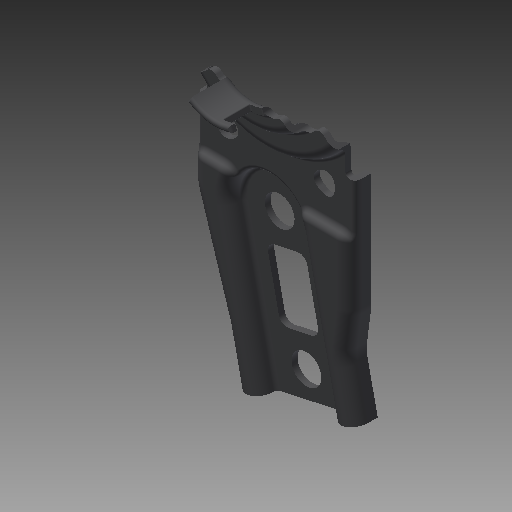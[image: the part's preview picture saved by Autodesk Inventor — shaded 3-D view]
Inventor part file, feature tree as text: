
AUTODESK INVENTOR PART (.ipt)
format: ipt  version: 2019 (Build 230136000, 136)  size: 857,088 bytes
history: native  units: mm
features: sketch x16, fillet x16, extrude x15, shell x1, hole x1, projected_geometry x1
ambient origin geometry x8: Origin, YZ Plane, XZ Plane, XY Plane, X Axis, Y Axis, Z Axis, Center Point
bodies: Solid1 (feature_tree)
feature tree (50):
  extrude  "Extrusion1"  Depth=8.726646mm
  sketch  "Sketch2"  dims[d3=17.27876mm d4=43.250017mm d5=79.522214mm d6=39.712729mm]
  extrude  "Extrusion3"  Depth=43.250017mm
  fillet  "Fillet2"  Radius=79.522214mm
  fillet  "Fillet3"  Radius=39.712729mm
  extrude  "Extrusion4"  Depth=128.300719mm
  fillet  "Fillet4"  Radius=154.593836mm
  fillet  "Fillet5"  Radius=27.808099mm
  fillet  "Fillet6"  Radius=114.918982mm
  fillet  "Fillet7"  Radius=141.5725mm
  shell  "Shell1"  Thickness=22.272111mm
  fillet  "Fillet8"  Radius=22.8461mm
  extrude  "Extrusion5"  Depth=22.90243mm
  extrude  "Extrusion6"  Depth=14.2mm TaperAngle=0.0deg
  fillet  "Fillet9"  Radius=60.635116mm
  fillet  "Fillet10"  Radius=36.044812mm
  extrude  "Extrusion7"  Depth=8.2mm TaperAngle=0.0deg
  extrude  "Extrusion8"  Depth=6.33mm
  extrude  "Extrusion9"  Depth=3.0mm
  extrude  "Extrusion10"  Depth=2.0mm
  extrude  "Extrusion11"  Depth=1.0mm
  fillet  "Fillet11"  Radius=1.0mm
  extrude  "Extrusion12"  Depth=37.0mm
  extrude  "Extrusion13"  Depth=5.0mm
  fillet  "Fillet14"  Radius=3.15mm
  fillet  "Fillet12"  Radius=3.0mm
  fillet  "Fillet15"  Radius=1.68mm
  extrude  "Extrusion14"  Depth=3.0mm
  hole  "Hole1"  [1 undecoded]
  extrude  "Extrusion15"  Depth=3.0mm
  extrude  "Extrusion16"  Depth=0.5mm
  fillet  "Fillet16"  Radius=3.0mm
  fillet  "Fillet17"  Radius=6.422812mm
  fillet  "Fillet18"  Radius=6.422812mm
  sketch  "Sketch1"  dims[d0=17.27876mm d1=39.728969mm d2=8.726646mm]
  sketch  "Sketch3"  dims[d7=74.67218mm d8=128.300719mm d9=154.593836mm d10=27.808099mm d11=114.918982mm d12=141.5725mm d13=22.272111mm d14=22.8461mm]
  sketch  "Sketch4"  dims[d15=94.54884mm d16=22.90243mm]
  sketch  "Sketch5"  dims[d17=37.177966mm d18=14.2mm d19=0.0mm d20=60.635116mm d23=36.044812mm]
  projected_geometry  "Projected Loop1"
  sketch  "Sketch6"  dims[d24=73.417911mm d26=8.2mm d27=0.0mm]
  sketch  "Sketch7"  dims[d29=20.0mm d30=6.33mm]
  sketch  "Sketch8"  dims[d31=3.15mm d32=0.0mm d33=3.0mm]
  sketch  "Sketch9"  dims[d34=2.0mm d35=2.0mm]
  sketch  "Sketch11"  dims[d36=3.0mm d37=2.0mm d38=1.0mm]
  sketch  "Sketch12"  dims[d39=37.0mm d40=37.0mm]
  sketch  "Sketch13"  dims[d41=5.0mm d42=5.0mm d43=3.15mm d44=0.0mm d45=3.0mm d46=0.0mm d47=1.68mm]
  sketch  "Sketch15"  dims[d48=1.95mm d49=3.0mm]
  sketch  "Sketch16"  dims[d50=5.55mm d51=0.0mm d52=10.0mm]
  sketch  "Sketch17"  dims[d53=3.0mm d54=0.0mm d55=3.0mm]
  sketch  "Sketch18"  dims[d56=10.15mm d57=0.0mm d58=6.8mm d61=3.0mm d62=0.0mm d63=6.422812mm d64=6.422812mm d65=3.0mm d66=10.053096mm d67=21.25mm d68=0.0mm d69=5.0mm d70=2.0mm d71=21.25mm d72=0.0mm d73=21.25mm d74=0.0mm d75=3.0mm d77=1.375mm d78=2.0mm d79=10.0mm d80=0.0mm d81=63.5mm d82=15.0mm d83=6.0mm d84=4.0mm d85=2.0mm d86=90.0deg d87=8.0mm d88=20.594885mm d89=6.0mm d90=6.0mm d91=15.0mm d92=15.0mm d93=4.0mm d94=10.0mm d95=0.0mm d96=13.0mm d97=6.0mm d98=0.0mm d99=1.0mm d100=0.5mm d101=0.5mm d102=0.5mm]
note: 1 required parameter value undecoded (feature->parameter linkage not recoverable at this tier; creation-order binding heuristic only, values carry confidence <= 0.55)
